# Revit family: Square_Table-Teknion-CWTQP_C-D_Extended_Knife_Edge-R2020
name_source: partatom
category: Furniture
units: mm (PartAtom-declared; Revit-internal decimal feet)

## family parameters
Always vertical = Yes
Cut with Voids When Loaded = No
OmniClass Number = 23.40.20.00
OmniClass Title = General Furniture and Specialties
Room Calculation Point = No
Shared = Yes
Work Plane-Based = No

## types (2) — shared parameters
Assembly Code = E2020200
Available Size = 66, 72, 78, 84 and 90 inches
Height = 29.004 "
Manufacturer = Teknion
Manufacturer Fax = 416.661.4586
Part Number = CWTQP
Product Documentation Link = https://www.teknion.com
Product Line = C+D
Product Page URL = https://www.teknion.com
Series = Custom Wood
Sustainability Data = https://www.teknion.com
URL = www.teknion.com
Unit Weight URL = http://www.teknion.com
Warranty = http://www.teknion.com
zero-valued in all types: Default Elevation

## per-type parameters (varying)
| type | Description | Model |
| Open Leg Base | Custom Wood C+D Square Table, Extended Knife Edge, Open Leg Base | CWTQPB__ |
| Standard Base with Central Plinth | Custom Wood C+D Square Table, Extended Knife Edge, Standard Base with Central Plinth | CWTQPP__ |

type visibility flags: 2 boolean params named "<type name>" — each type sets only its own to Yes (folded from table)

## geometry (parser evidence)
native form markers: Sweep x3
no freeform markers — native parametric forms only
